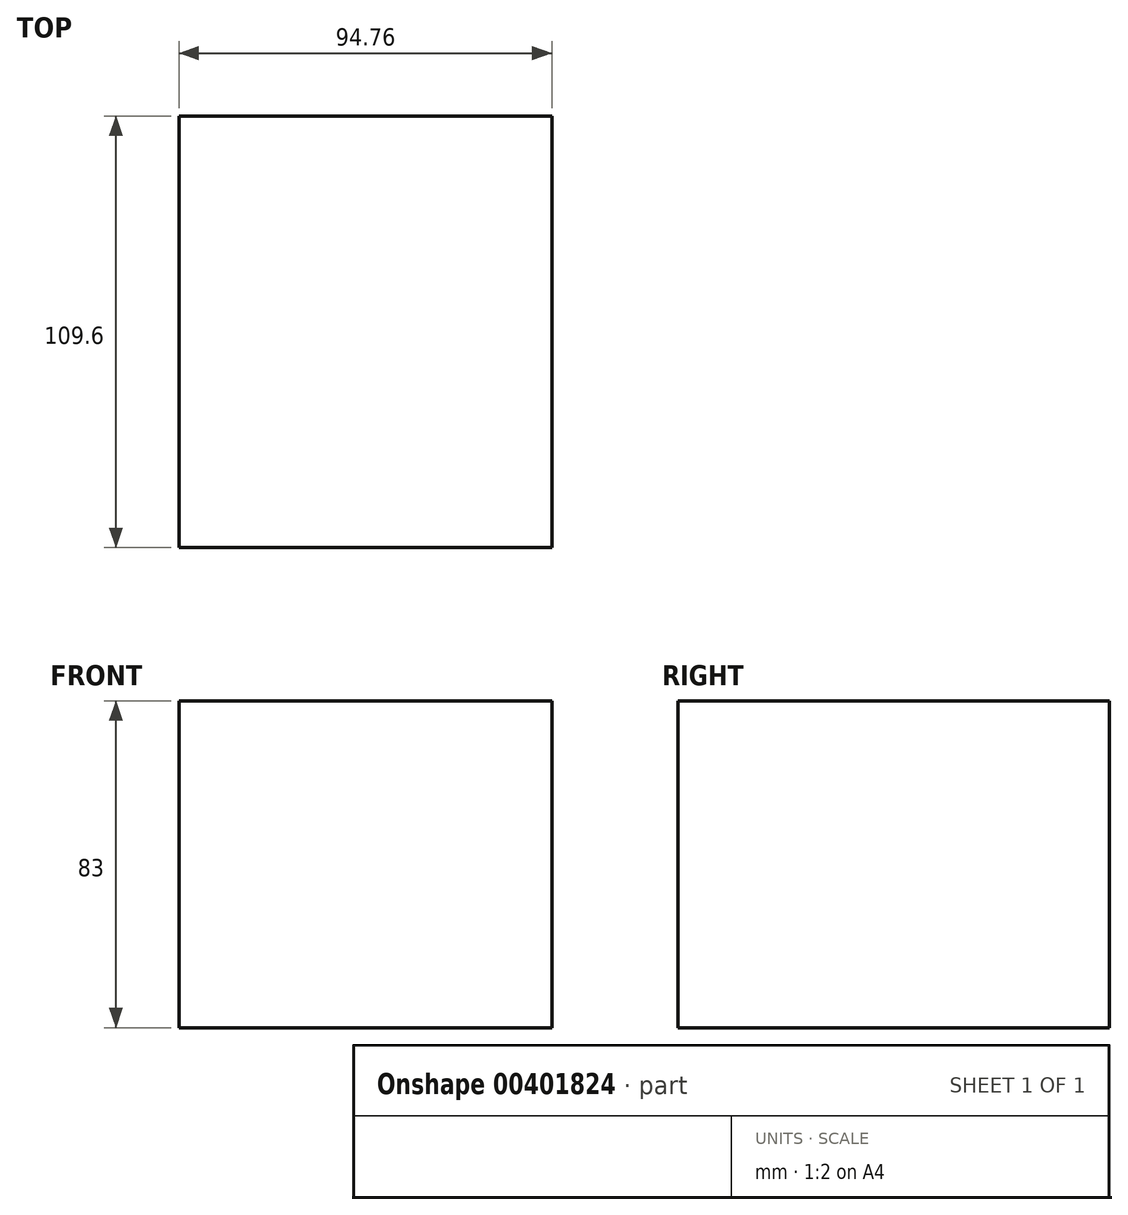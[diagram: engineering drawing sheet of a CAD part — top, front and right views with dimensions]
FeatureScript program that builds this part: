
annotation { "Feature Type Name" : "Feature", "Feature Type Description" : "" }
export const myFeature = defineFeature(function(context is Context, id is Id, definition is map)
    precondition{}
    {
        {
            var Q0;
            Q0=qCreatedBy(makeId("Top.planeOp"),FACE);
            var sketch = newSketch(context, id + "F0", { "sketchPlane" : qUnion([Q0])});
            skLineSegment(sketch, "E0.bottom", {"start": v(-47.37, 54.8) * mm, "end": v(47.38, 54.8) * mm});
            skLineSegment(sketch, "E0.top", {"start": v(-47.38, -54.8) * mm, "end": v(47.37, -54.8) * mm});
            skLineSegment(sketch, "E0.left", {"start": v(-47.37, 54.8) * mm, "end": v(-47.38, -54.8) * mm});
            skLineSegment(sketch, "E0.right", {"start": v(47.38, 54.8) * mm, "end": v(47.37, -54.8) * mm});
            skPoint(sketch, "E0.middle", {"position": v(0, 0) * mm});
            skSolve(sketch);
        }
        {
            var Q0;
            Q0 = qSketchRegion(id + "F0", true);
            extrude(context, id + "F1", {"entities" : qUnion([Q0]), "depth" : 83 * mm});
        }
    });
